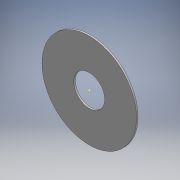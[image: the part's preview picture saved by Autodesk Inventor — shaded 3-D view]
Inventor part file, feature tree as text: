
AUTODESK INVENTOR PART (.ipt)
format: ipt  version: 2016 (Build 200138000, 138)  size: 92,672 bytes
history: native  units: mm
features: sketch x2, extrude x1
ambient origin geometry x8: Origin, YZ Plane, XZ Plane, XY Plane, X Axis, Y Axis, Z Axis, Center Point
bodies: Solid1 (feature_tree)
feature tree (3):
  sketch  "Sketch1"  dims[d0=305.0mm d1=100.0mm]
  extrude  "Extrusion1"  Depth=100.0mm
  sketch  "Sketch2"  dims[d2=5.0mm d3=0.0mm]
